# Revit family: 202_Bistro-E
name_source: partatom
category: Air Terminals
revit_build: Autodesk Revit 2018 (Build: 20170223_1515(x64)
units: mm (PartAtom-declared; Revit-internal decimal feet)

## family parameters
Always vertical = Yes
Cut with Voids When Loaded = No
Part Type = Normal
Room Calculation Point = Yes
Round Connector Dimension = Use Diameter
Shared = No
Work Plane-Based = No

## types (1)
- 125-13626
    CAT0 = Yes
    CLBTZ = 0 mm  [stored 0 ft]
    CL_Location_5000 = 5000 mm  [stored 16.4042 ft]
    D = 125 mm
    Description = Kitchen hood Bistro-E/F
    H_ARR = 0 mm  [stored 0 ft]
    L_ARR = 400 mm  [stored 1.31234 ft]
    MC Product Code = 125-13626
    Manufacturer = Flexit
    QmdConnectorList = 201;D
    W_ARR = 400 mm  [stored 1.31234 ft]
    X1 = 221 mm  [stored 0.725066 ft]
    X2 = 68 mm  [stored 0.223097 ft]
    X3 = 206 mm  [stored 0.675853 ft]
    XRefLineVPlnId = 7453
    Y1 = 146 mm  [stored 0.479003 ft]
    Y2 = 45 mm  [stored 0.147638 ft]
    Y3 = 131 mm  [stored 0.42979 ft]
    YRefLineVPlnId = 7456
    Z1 = 90 mm  [stored 0.295276 ft]
    Z1__ve = -90 mm  [stored -0.295276 ft]
    Z2 = 30 mm  [stored 0.0984252 ft]
    magiPartTypeId = 202
    magiProductFamilyId = Bistro-E
    magiProductId = Bistro-E 125

note: [stored X ft] marks values corroborated as IEEE doubles in the binary element streams (Revit-internal decimal feet)

## geometry (parser evidence)
native form markers: Sweep x2
no freeform markers — native parametric forms only
